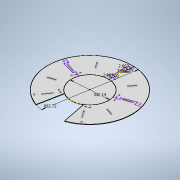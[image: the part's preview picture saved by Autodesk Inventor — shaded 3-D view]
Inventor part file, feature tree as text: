
AUTODESK INVENTOR PART (.ipt)
format: ipt  version: 2020 (Build 240168000, 168)  size: 592,896 bytes
history: native  units: mm
features: extrude x6, sketch x5, pattern_circular x4, mirror x3, plane x1
ambient origin geometry x8: Origin, YZ Plane, XZ Plane, XY Plane, X Axis, Y Axis, Z Axis, Center Point
bodies: Body1 (feature_tree)
feature tree (19):
  extrude  "Extrusion3"  Depth=6.5mm
  extrude  "Extrusion4"  Depth=2.666667mm
  extrude  "Extrusion5"  Depth=1.333333mm
  sketch  "Sketch5"  dims[d25=2.666667mm d32=1.333333mm]
  extrude  "Extrusion7"  TaperAngle=0.0deg  [1 undecoded]
  sketch  "Sketch7"  dims[d40=3.25mm d41=90.0deg d42=3.25mm d43=90.0deg d47=50.0mm d49=360.0deg d52=4.363323mm d54=10.0mm d55=0.0mm d60=0.872665mm d61=12.566371mm d62=13.439035mm d63=2.666667mm d64=0.523599mm d66=0.523599mm d67=2.666667mm d68=2.666667mm d70=12.566371mm d71=12.566371mm d84=300.14mm d85=682.72mm d86=491.43mm d87=150.07mm d88=341.36mm d89=4.363323mm d90=1.919862mm d91=1.919862mm d94=300.14mm d95=682.72mm d96=0.24305mm d104=6.5mm d105=12.0mm d108=1.333333mm d109=1.333333mm d110=1.333333mm d111=1.333333mm d112=0.0mm d113=0.0mm d114=0.0mm d116=1.333333mm d117=1.333333mm d119=1.333333mm d120=1.333333mm d121=6.5mm d122=10.0mm d123=0.0mm d124=0.0mm d126=1.09mm d127=16.333333mm d128=1.333333mm d129=1.333333mm d130=1.333333mm d131=1.333333mm d132=6.5mm d133=10.0mm d135=0.523599mm d137=0.0mm d138=0.0mm d140=0.666667mm d141=3.25mm d142=20.0mm d143=12.566371mm d145=20.0mm d146=12.566371mm d148=0.27mm d149=145.0mm d150=90.0deg d151=90.0deg d152=90.0deg d153=90.0deg d154=20.0mm d155=25.132741mm d157=20.0mm d158=25.132741mm]
  extrude  "Extrusion8"  TaperAngle=90.0deg  [1 undecoded]
  extrude  "Extrusion9"  Depth=145.0mm
  plane  "Work Plane1"
  mirror  "Mirror2"
  mirror  "Mirror1"
  pattern_circular  "Circular Pattern1"  Angle=90.0deg  [1 undecoded]
  pattern_circular  "Circular Pattern2"  Count=5 Angle=360.0deg
  pattern_circular  "Circular Pattern3"  [2 undecoded]
  mirror  "Mirror3"
  pattern_circular  "Circular Pattern4"  [2 undecoded]
  sketch  "Sketch2"  dims[d15=6.0mm d16=0.0mm d21=6.5mm]
  sketch  "Sketch3"  dims[d23=66.666667mm d24=2.666667mm]
  sketch  "Sketch6"  dims[d33=1.333333mm d38=0.0mm d39=0.0mm]
note: 7 required parameter values undecoded (feature->parameter linkage not recoverable at this tier; creation-order binding heuristic only, values carry confidence <= 0.55)
